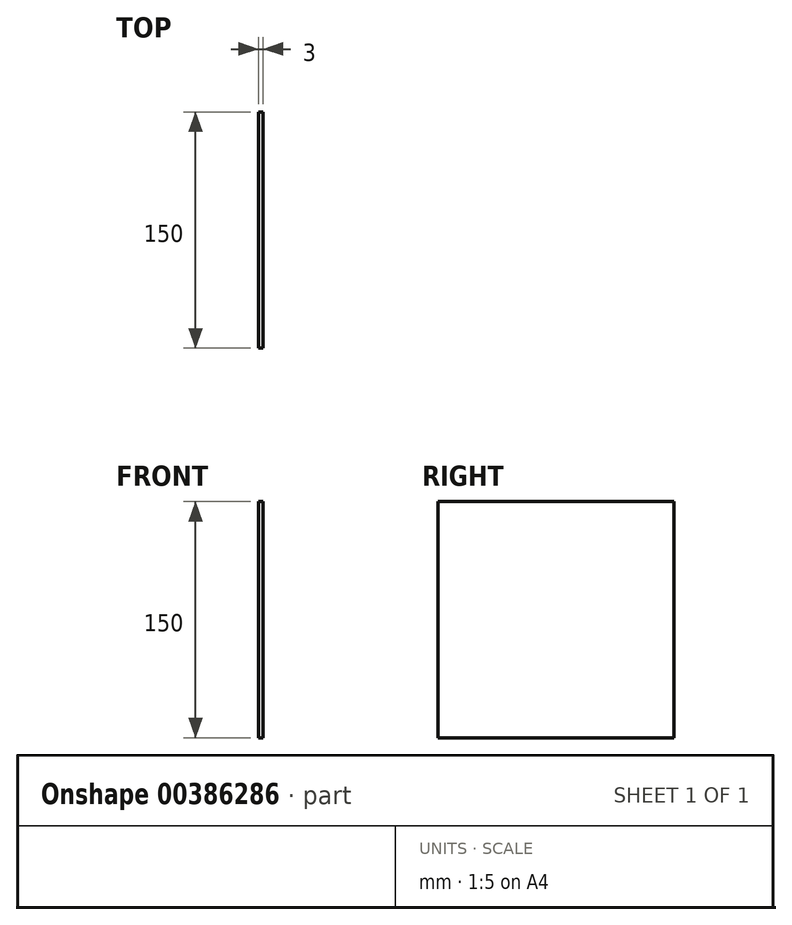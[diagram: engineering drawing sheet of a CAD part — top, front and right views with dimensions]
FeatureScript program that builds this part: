
annotation { "Feature Type Name" : "Feature", "Feature Type Description" : "" }
export const myFeature = defineFeature(function(context is Context, id is Id, definition is map)
    precondition{}
    {
        {
            var Q0;
            Q0=qCreatedBy(makeId("Right.planeOp"),FACE);
            var sketch = newSketch(context, id + "F0", { "sketchPlane" : qUnion([Q0])});
            skLineSegment(sketch, "E0.bottom", {"start": v(-81.46, 109.16) * mm, "end": v(68.54, 109.16) * mm});
            skLineSegment(sketch, "E0.top", {"start": v(-81.46, -40.84) * mm, "end": v(68.54, -40.84) * mm});
            skLineSegment(sketch, "E0.left", {"start": v(-81.46, 109.16) * mm, "end": v(-81.46, -40.84) * mm});
            skLineSegment(sketch, "E0.right", {"start": v(68.54, 109.16) * mm, "end": v(68.54, -40.84) * mm});
            skSolve(sketch);
        }
        {
            var Q0;
            Q0 = qSketchRegion(id + "F0", true);
            extrude(context, id + "F1", {"entities" : qUnion([Q0]), "depth" : 3 * mm});
        }
    });
